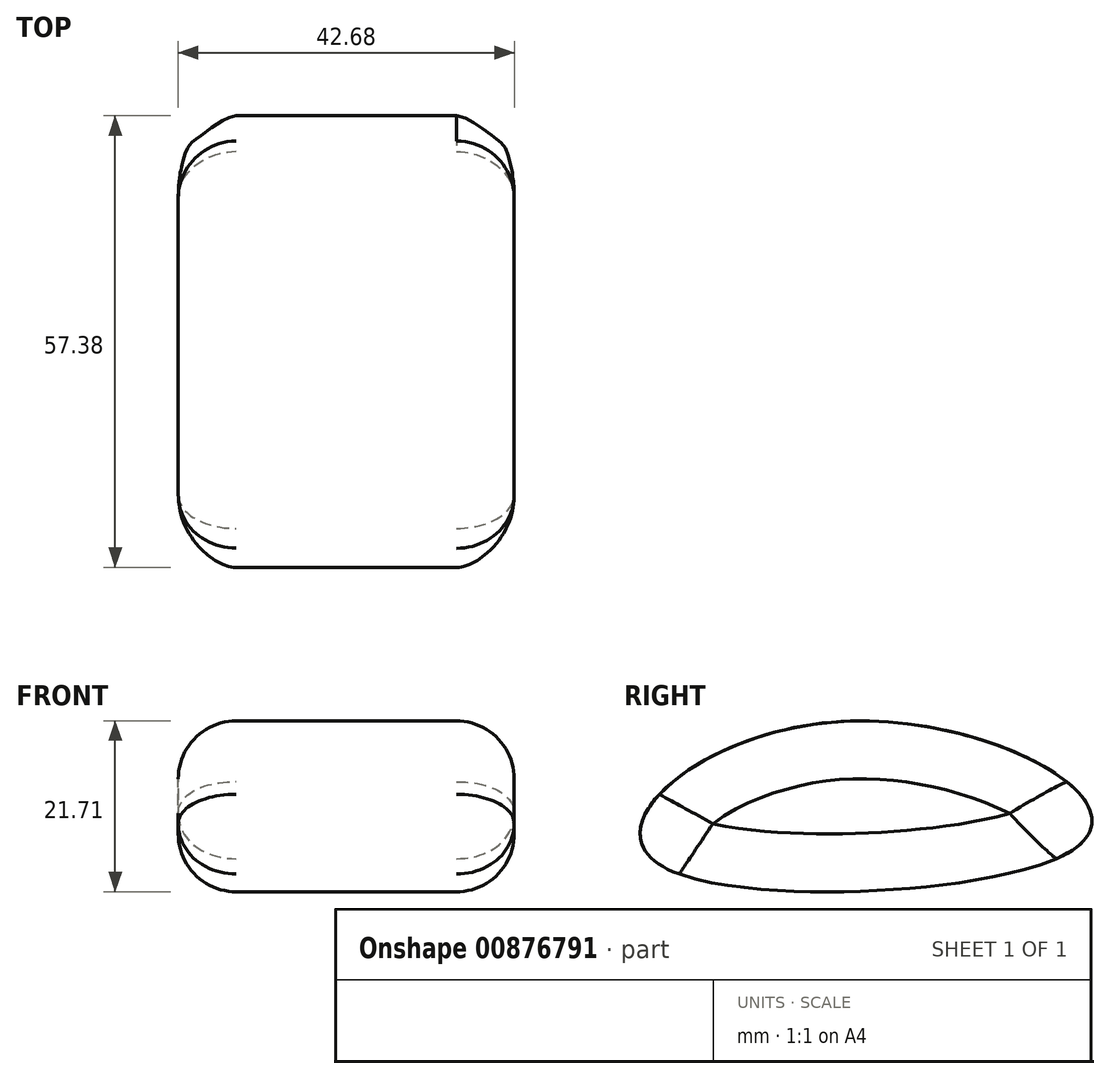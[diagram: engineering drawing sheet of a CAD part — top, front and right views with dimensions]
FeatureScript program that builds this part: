
annotation { "Feature Type Name" : "Feature", "Feature Type Description" : "" }
export const myFeature = defineFeature(function(context is Context, id is Id, definition is map)
    precondition{}
    {
        {
            var Q0;
            Q0=qCreatedBy(makeId("Right.planeOp"),FACE);
            var sketch = newSketch(context, id + "F0", { "sketchPlane" : qUnion([Q0])});
            skFitSpline(sketch, "E0", {"points": [v(-41.06, 5.26) * mm, v(-16.1, 16.7) * mm, v(14.29, 7.07) * mm, v(12.48, 0) * mm, v(-38.05, -2.26) * mm, v(-41.06, 5.26) * mm]});
            skSolve(sketch);
        }
        {
            var Q0;
            Q0=makeQuery(id+"F0.imprint","IMPRINT",FACE,{"disambiguationData":[TD([[makeQuery(id+"F0.imprint","IMPRINT",EDGE,{"derivedFrom":sQuery(id+"F0.wireOp",EDGE,"E0")}),-1.0]])]});
            extrude(context, id + "F1", {"entities" : qUnion([Q0]), "endBound" : BoundingType.SYMMETRIC, "depth" : 42.67 * mm, "offsetDistance" : 25.4 * mm});
        }
        {
            var Q0;
            Q0=makeQuery(id+"F1.opExtrude","CAP_EDGE",EDGE,{"disambiguationData":[OSD([sQuery(id+"F0.wireOp",EDGE,"E0")])],"isStart":true});
            var Q1;
            Q1=makeQuery(id+"F1.opExtrude","CAP_EDGE",EDGE,{"disambiguationData":[OSD([sQuery(id+"F0.wireOp",EDGE,"E0")])],"isStart":false});
            fillet(context, id + "F2", {"entities" : qUnion([Q0, Q1]), "radius" : 7.36 * mm, "tangentPropagation" : true, "allowEdgeOverflow" : false});
        }
    });
